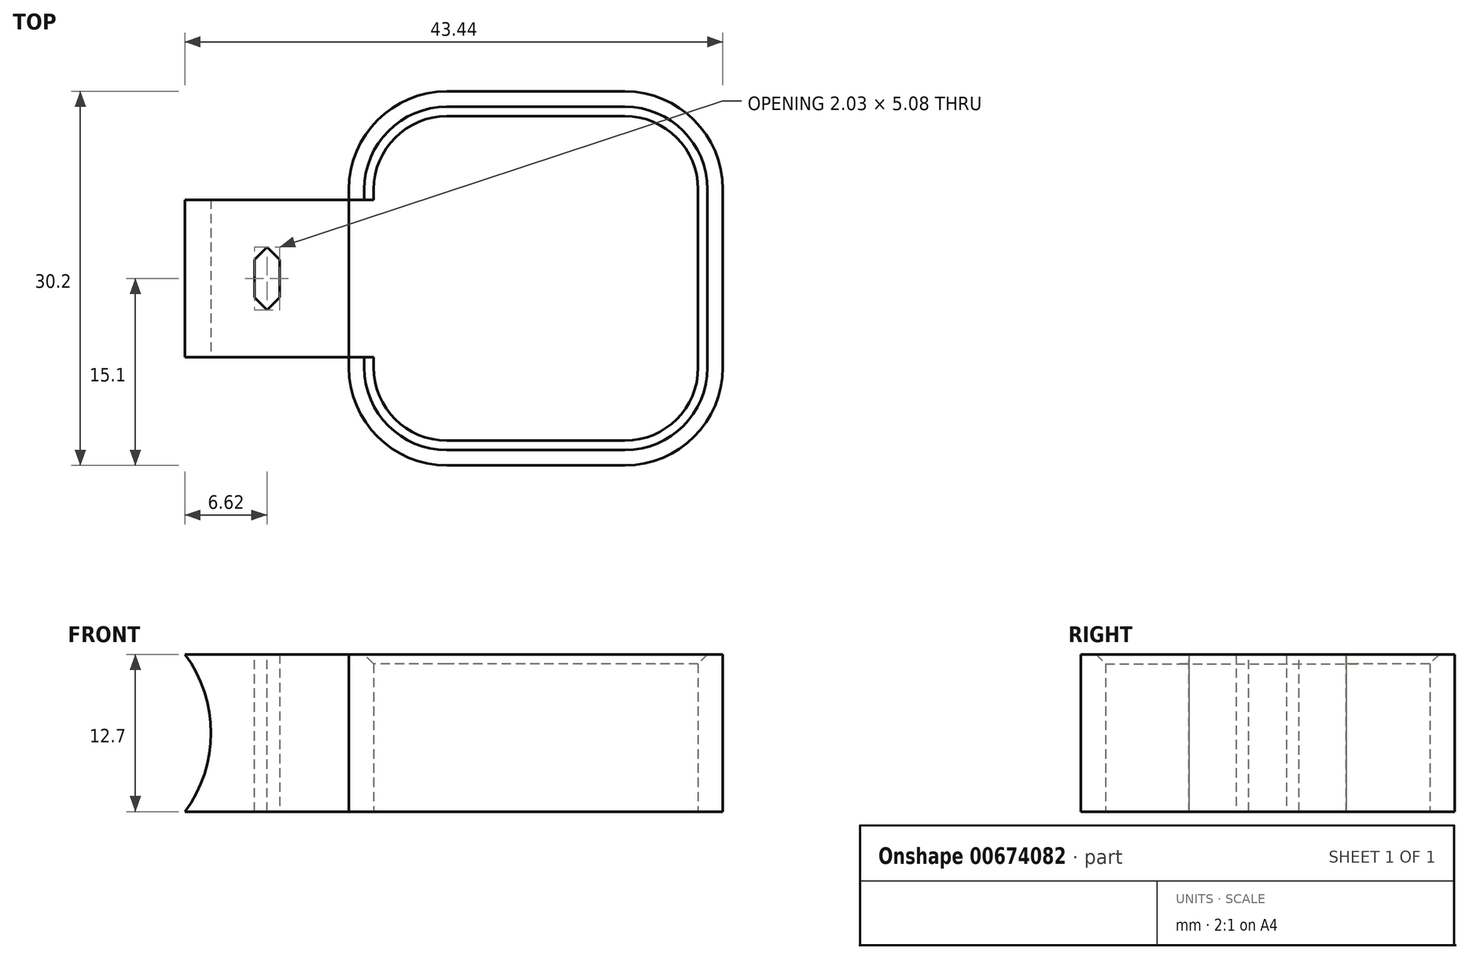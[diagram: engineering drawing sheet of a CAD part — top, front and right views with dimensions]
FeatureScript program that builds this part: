
annotation { "Feature Type Name" : "Feature", "Feature Type Description" : "" }
export const myFeature = defineFeature(function(context is Context, id is Id, definition is map)
    precondition{}
    {
        {
            var Q0;
            Q0=qCreatedBy(makeId("Top.planeOp"),FACE);
            var sketch = newSketch(context, id + "F0", { "sketchPlane" : qUnion([Q0])});
            skCircle(sketch, "E0.cCircle", {"center": v(0, 0) * mm, "radius": 11 * mm, "construction": true});
            skLineSegment(sketch, "E0.0", {"start": v(-7.2, 11) * mm, "end": v(7.2, 11) * mm, "construction": true});
            skLineSegment(sketch, "E0.1", {"start": v(11, 7.2) * mm, "end": v(11, -7.2) * mm, "construction": true});
            skLineSegment(sketch, "E0.2", {"start": v(7.2, -11) * mm, "end": v(-7.2, -11) * mm, "construction": true});
            skLineSegment(sketch, "E0.3", {"start": v(-11, -7.2) * mm, "end": v(-11, 7.2) * mm, "construction": true});
            skPoint(sketch, "E0.0.midPoint", {"position": v(0, 11) * mm});
            skPoint(sketch, "E1.visualSharp", {"position": v(-11, 11) * mm});
            skArc(sketch, "E1.filletArc", {"start": v(-7.19, 11) * mm, "mid": v(-9.88, 9.88) * mm, "end": v(-11, 7.2) * mm, "construction": true});
            skPoint(sketch, "E2.visualSharp", {"position": v(11, 11) * mm});
            skArc(sketch, "E2.filletArc", {"start": v(11, 7.2) * mm, "mid": v(9.88, 9.88) * mm, "end": v(7.2, 11) * mm, "construction": true});
            skPoint(sketch, "E3.visualSharp", {"position": v(11, -11) * mm});
            skArc(sketch, "E3.filletArc", {"start": v(7.2, -11) * mm, "mid": v(9.88, -9.88) * mm, "end": v(11, -7.2) * mm, "construction": true});
            skPoint(sketch, "E4.visualSharp", {"position": v(-11, -11) * mm});
            skArc(sketch, "E4.filletArc", {"start": v(-11, -7.2) * mm, "mid": v(-9.88, -9.88) * mm, "end": v(-7.2, -11) * mm, "construction": true});
            skLineSegment(sketch, "E5.0", {"start": v(13.1, 7.2) * mm, "end": v(13.1, -7.19) * mm});
            skArc(sketch, "E5.1", {"start": v(7.2, -13.1) * mm, "mid": v(11.37, -11.37) * mm, "end": v(13.1, -7.2) * mm});
            skArc(sketch, "E5.2", {"start": v(13.1, 7.2) * mm, "mid": v(11.37, 11.37) * mm, "end": v(7.2, 13.1) * mm});
            skLineSegment(sketch, "E5.3", {"start": v(7.2, -13.1) * mm, "end": v(-7.2, -13.1) * mm});
            skLineSegment(sketch, "E5.4", {"start": v(-7.2, 13.1) * mm, "end": v(7.2, 13.1) * mm});
            skArc(sketch, "E5.5", {"start": v(-7.2, 13.1) * mm, "mid": v(-11.37, 11.37) * mm, "end": v(-13.1, 7.2) * mm});
            skLineSegment(sketch, "E5.6", {"start": v(-13.1, -7.19) * mm, "end": v(-13.1, 7.2) * mm});
            skArc(sketch, "E5.7", {"start": v(-13.1, -7.2) * mm, "mid": v(-11.37, -11.37) * mm, "end": v(-7.2, -13.1) * mm});
            skArc(sketch, "E6.0", {"start": v(-7.2, 15.1) * mm, "mid": v(-12.78, 12.78) * mm, "end": v(-15.1, 7.2) * mm});
            skLineSegment(sketch, "E6.1", {"start": v(-15.1, -7.19) * mm, "end": v(-15.1, 7.2) * mm});
            skLineSegment(sketch, "E6.2", {"start": v(-7.2, 15.1) * mm, "end": v(7.2, 15.1) * mm});
            skArc(sketch, "E6.3", {"start": v(-15.1, -7.2) * mm, "mid": v(-12.78, -12.78) * mm, "end": v(-7.2, -15.1) * mm});
            skArc(sketch, "E6.4", {"start": v(15.1, 7.2) * mm, "mid": v(12.78, 12.78) * mm, "end": v(7.2, 15.1) * mm});
            skLineSegment(sketch, "E6.5", {"start": v(15.1, 7.2) * mm, "end": v(15.1, -7.19) * mm});
            skArc(sketch, "E6.6", {"start": v(7.19, -15.1) * mm, "mid": v(12.78, -12.78) * mm, "end": v(15.1, -7.2) * mm});
            skLineSegment(sketch, "E6.7", {"start": v(7.19, -15.1) * mm, "end": v(-7.19, -15.1) * mm});
            skLineSegment(sketch, "E7.bottom", {"start": v(-13.1, -6.35) * mm, "end": v(-28.34, -6.35) * mm});
            skLineSegment(sketch, "E7.top", {"start": v(-13.1, 6.35) * mm, "end": v(-28.34, 6.35) * mm});
            skLineSegment(sketch, "E7.left", {"start": v(-13.1, -6.35) * mm, "end": v(-13.1, 6.35) * mm});
            skLineSegment(sketch, "E7.right", {"start": v(-28.34, -6.35) * mm, "end": v(-28.34, 6.35) * mm});
            skSolve(sketch);
        }
        {
            var Q0;
            {var subQ5=sQuery(id+"F0.wireOp",EDGE,"E7.left");Q0=makeQuery(id+"F0.imprint","IMPRINT",FACE,{"disambiguationData":[TD([[makeQuery(id+"F0.imprint","IMPRINT",EDGE,{"derivedFrom":subQ5}),1.0]])]});}
            var Q1;
            {var subQ5=sQuery(id+"F0.wireOp",EDGE,"E7.right");Q1=makeQuery(id+"F0.imprint","IMPRINT",FACE,{"disambiguationData":[TD([[makeQuery(id+"F0.imprint","IMPRINT",EDGE,{"derivedFrom":subQ5}),-1.0]])]});}
            var Q2;
            Q2=makeQuery(id+"F0.imprint","IMPRINT",FACE,{"disambiguationData":[TD([[makeQuery(id+"F0.imprint","IMPRINT",EDGE,{"derivedFrom":sQuery(id+"F0.wireOp",EDGE,"E5.0")}),1.0]])]});
            extrude(context, id + "F1", {"entities" : qUnion([Q0, Q1, Q2]), "depth" : 12.7 * mm, "offsetDistance" : 25.4 * mm});
        }
        {
            var Q0;
            Q0=makeQuery(id+"F1.opExtrude","SWEPT_FACE",FACE,{"disambiguationData":[OSD([sQuery(id+"F0.wireOp",EDGE,"E7.bottom")])]});
            var sketch = newSketch(context, id + "F2", { "sketchPlane" : qUnion([Q0])});
            skCircle(sketch, "E8", {"center": v(-36.91, 6.35) * mm, "radius": 10.67 * mm});
            skSolve(sketch);
        }
        {
            var Q0;
            {var subQ1=sQuery(id+"F0.wireOp",EDGE,"E7.bottom");var subQ2=makeQuery(id+"F1.opExtrude","SWEPT_EDGE",EDGE,{"disambiguationData":[OSD([subQ1,sQuery(id+"F0.wireOp",EDGE,"E7.right")])]});Q0=makeQuery(id+"F2.imprint","IMPRINT",FACE,{"disambiguationData":[TD([[makeQuery(id+"F2.imprint","IMPRINT",EDGE,{"derivedFrom":subQ2}),1.0]])]});}
            var Q1;
            Q1=makeQuery(id+"F1.opExtrude","SWEPT_FACE",FACE,{"disambiguationData":[OSD([sQuery(id+"F0.wireOp",EDGE,"E7.top")])]});
            extrude(context, id + "F3", {"entities" : qUnion([Q0]), "operationType" : NewBodyOperationType.REMOVE, "endBound" : BoundingType.UP_TO_SURFACE, "oppositeDirection" : true, "depth" : 25.4 * mm, "endBoundEntityFace" : qUnion([Q1]), "offsetDistance" : 25.4 * mm});
        }
        {
            var Q0;
            Q0=makeQuery(id+"F1.opExtrude","CAP_FACE",FACE,{"disambiguationData":[OSD([sQuery(id+"F0.wireOp",EDGE,"E5.0"),sQuery(id+"F0.wireOp",EDGE,"E5.1"),sQuery(id+"F0.wireOp",EDGE,"E5.2"),sQuery(id+"F0.wireOp",EDGE,"E5.3"),sQuery(id+"F0.wireOp",EDGE,"E5.4"),sQuery(id+"F0.wireOp",EDGE,"E5.5"),sQuery(id+"F0.wireOp",EDGE,"E5.6"),sQuery(id+"F0.wireOp",EDGE,"E5.7"),sQuery(id+"F0.wireOp",EDGE,"E6.0"),sQuery(id+"F0.wireOp",EDGE,"E6.1"),sQuery(id+"F0.wireOp",EDGE,"E6.2"),sQuery(id+"F0.wireOp",EDGE,"E6.3"),sQuery(id+"F0.wireOp",EDGE,"E6.4"),sQuery(id+"F0.wireOp",EDGE,"E6.5"),sQuery(id+"F0.wireOp",EDGE,"E6.6"),sQuery(id+"F0.wireOp",EDGE,"E6.7"),sQuery(id+"F0.wireOp",EDGE,"E7.bottom"),sQuery(id+"F0.wireOp",EDGE,"E7.top"),sQuery(id+"F0.wireOp",EDGE,"E7.left"),sQuery(id+"F0.wireOp",EDGE,"E7.right")])],"isStart":false});
            var sketch = newSketch(context, id + "F4", { "sketchPlane" : qUnion([Q0])});
            skPoint(sketch, "E9", {"position": v(-21.72, 0) * mm});
            skPoint(sketch, "E9.positionSnap0", {"position": v(-21.72, -6.35) * mm});
            skLineSegment(sketch, "E10.bottom", {"start": v(-22.74, 2.54) * mm, "end": v(-20.7, 2.54) * mm});
            skLineSegment(sketch, "E10.top", {"start": v(-22.74, -2.54) * mm, "end": v(-20.7, -2.54) * mm});
            skLineSegment(sketch, "E10.left", {"start": v(-22.74, 2.54) * mm, "end": v(-22.74, -2.54) * mm});
            skLineSegment(sketch, "E10.right", {"start": v(-20.7, 2.54) * mm, "end": v(-20.7, -2.54) * mm});
            skSolve(sketch);
        }
        {
            var Q0;
            Q0=makeQuery(id+"F4.imprint","IMPRINT",FACE,{"disambiguationData":[TD([[makeQuery(id+"F4.imprint","IMPRINT",EDGE,{"derivedFrom":sQuery(id+"F4.wireOp",EDGE,"E10.bottom")}),-1.0]])]});
            var Q1;
            Q1=makeQuery(id+"F1.opExtrude","CAP_FACE",FACE,{"disambiguationData":[OSD([sQuery(id+"F0.wireOp",EDGE,"E5.0"),sQuery(id+"F0.wireOp",EDGE,"E5.1"),sQuery(id+"F0.wireOp",EDGE,"E5.2"),sQuery(id+"F0.wireOp",EDGE,"E5.3"),sQuery(id+"F0.wireOp",EDGE,"E5.4"),sQuery(id+"F0.wireOp",EDGE,"E5.5"),sQuery(id+"F0.wireOp",EDGE,"E5.6"),sQuery(id+"F0.wireOp",EDGE,"E5.7"),sQuery(id+"F0.wireOp",EDGE,"E6.0"),sQuery(id+"F0.wireOp",EDGE,"E6.1"),sQuery(id+"F0.wireOp",EDGE,"E6.2"),sQuery(id+"F0.wireOp",EDGE,"E6.3"),sQuery(id+"F0.wireOp",EDGE,"E6.4"),sQuery(id+"F0.wireOp",EDGE,"E6.5"),sQuery(id+"F0.wireOp",EDGE,"E6.6"),sQuery(id+"F0.wireOp",EDGE,"E6.7"),sQuery(id+"F0.wireOp",EDGE,"E7.bottom"),sQuery(id+"F0.wireOp",EDGE,"E7.top"),sQuery(id+"F0.wireOp",EDGE,"E7.left"),sQuery(id+"F0.wireOp",EDGE,"E7.right")])],"isStart":true});
            extrude(context, id + "F5", {"entities" : qUnion([Q0]), "operationType" : NewBodyOperationType.REMOVE, "endBound" : BoundingType.UP_TO_SURFACE, "oppositeDirection" : true, "depth" : 25.4 * mm, "endBoundEntityFace" : qUnion([Q1]), "offsetDistance" : 25.4 * mm});
        }
        {
            var Q0;
            Q0=makeQuery(id+"F5.boolean.opBoolean","COPY",EDGE,{"derivedFrom":makeQuery(id+"F5.opExtrude","SWEPT_EDGE",EDGE,{"disambiguationData":[OSD([sQuery(id+"F4.wireOp",EDGE,"E10.top"),sQuery(id+"F4.wireOp",EDGE,"E10.left")])]})});
            var Q1;
            Q1=makeQuery(id+"F5.boolean.opBoolean","COPY",EDGE,{"derivedFrom":makeQuery(id+"F5.opExtrude","SWEPT_EDGE",EDGE,{"disambiguationData":[OSD([sQuery(id+"F4.wireOp",EDGE,"E10.top"),sQuery(id+"F4.wireOp",EDGE,"E10.right")])]})});
            var Q2;
            Q2=makeQuery(id+"F5.boolean.opBoolean","COPY",EDGE,{"derivedFrom":makeQuery(id+"F5.opExtrude","SWEPT_EDGE",EDGE,{"disambiguationData":[OSD([sQuery(id+"F4.wireOp",EDGE,"E10.bottom"),sQuery(id+"F4.wireOp",EDGE,"E10.right")])]})});
            var Q3;
            Q3=makeQuery(id+"F5.boolean.opBoolean","COPY",EDGE,{"derivedFrom":makeQuery(id+"F5.opExtrude","SWEPT_EDGE",EDGE,{"disambiguationData":[OSD([sQuery(id+"F4.wireOp",EDGE,"E10.bottom"),sQuery(id+"F4.wireOp",EDGE,"E10.left")])]})});
            chamfer(context, id + "F6", {"entities" : qUnion([Q0, Q1, Q2, Q3]), "width" : 1.02 * mm, "tangentPropagation" : true});
        }
        {
            var Q0;
            Q0=makeQuery(id+"F1.opExtrude","CAP_EDGE",EDGE,{"disambiguationData":[OSD([sQuery(id+"F0.wireOp",EDGE,"E5.7")])],"isStart":false});
            var Q1;
            Q1=makeQuery(id+"F1.opExtrude","CAP_EDGE",EDGE,{"disambiguationData":[OSD([sQuery(id+"F0.wireOp",EDGE,"E5.3")])],"isStart":false});
            var Q2;
            Q2=makeQuery(id+"F1.opExtrude","CAP_EDGE",EDGE,{"disambiguationData":[OSD([sQuery(id+"F0.wireOp",EDGE,"E5.6"),sQuery(id+"F0.wireOp",EDGE,"E7.left")])],"isStart":false});
            var Q3;
            Q3=makeQuery(id+"F1.opExtrude","CAP_EDGE",EDGE,{"disambiguationData":[OSD([sQuery(id+"F0.wireOp",EDGE,"E5.5")])],"isStart":false});
            var Q4;
            Q4=makeQuery(id+"F1.opExtrude","CAP_EDGE",EDGE,{"disambiguationData":[OSD([sQuery(id+"F0.wireOp",EDGE,"E5.4")])],"isStart":false});
            var Q5;
            Q5=makeQuery(id+"F1.opExtrude","CAP_EDGE",EDGE,{"disambiguationData":[OSD([sQuery(id+"F0.wireOp",EDGE,"E5.2")])],"isStart":false});
            var Q6;
            Q6=makeQuery(id+"F1.opExtrude","CAP_EDGE",EDGE,{"disambiguationData":[OSD([sQuery(id+"F0.wireOp",EDGE,"E5.0")])],"isStart":false});
            var Q7;
            Q7=makeQuery(id+"F1.opExtrude","CAP_EDGE",EDGE,{"disambiguationData":[OSD([sQuery(id+"F0.wireOp",EDGE,"E5.1")])],"isStart":false});
            chamfer(context, id + "F7", {"entities" : qUnion([Q0, Q1, Q2, Q3, Q4, Q5, Q6, Q7]), "width" : 0.76 * mm, "tangentPropagation" : true});
        }
    });
